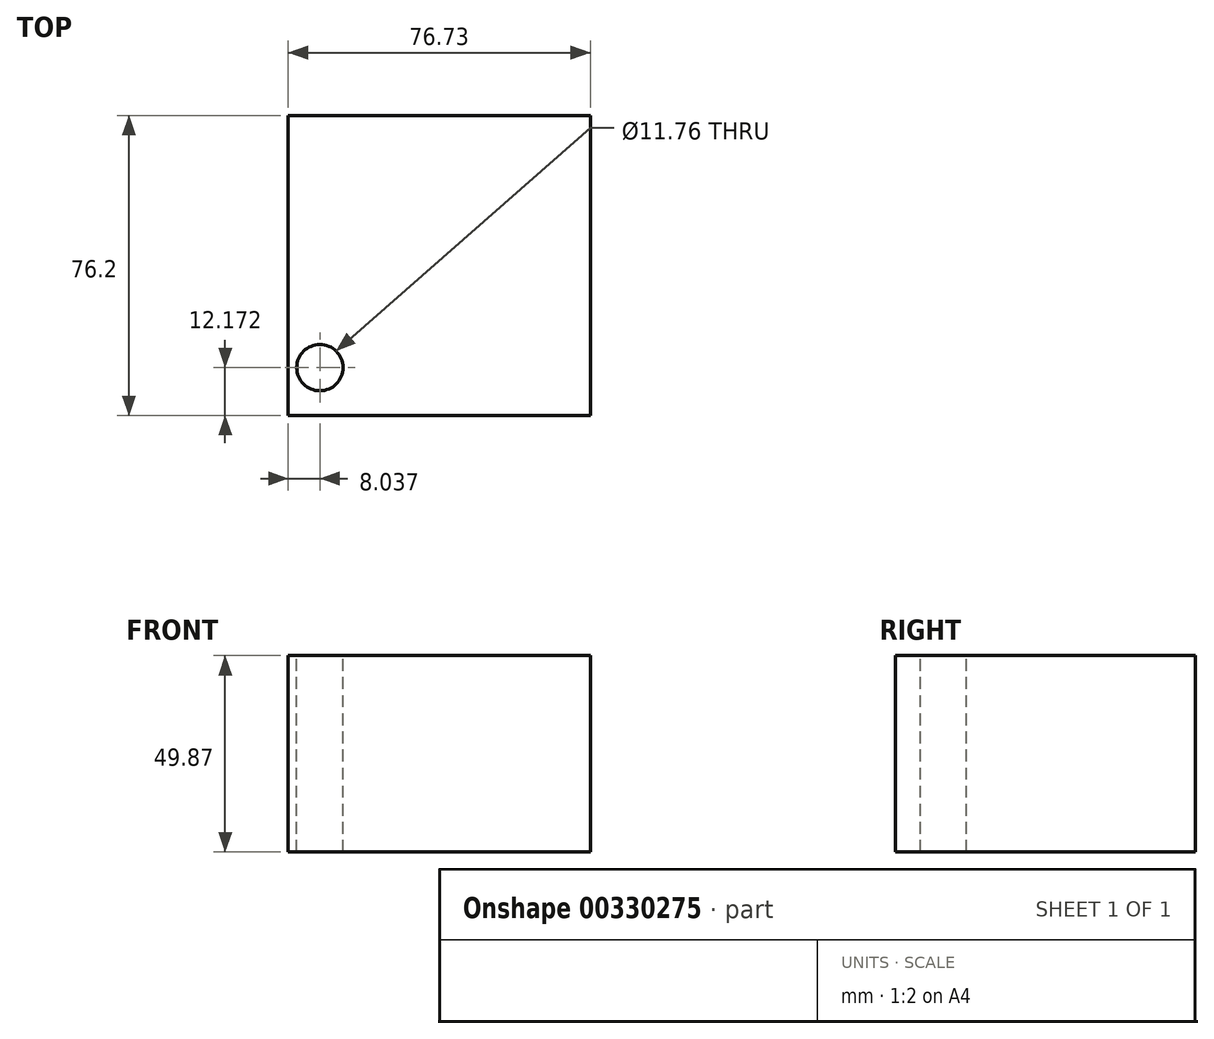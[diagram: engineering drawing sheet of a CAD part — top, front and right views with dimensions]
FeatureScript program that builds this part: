
annotation { "Feature Type Name" : "Feature", "Feature Type Description" : "" }
export const myFeature = defineFeature(function(context is Context, id is Id, definition is map)
    precondition{}
    {
        {
            var Q0;
            Q0=qCreatedBy(makeId("Front.planeOp"),FACE);
            var sketch = newSketch(context, id + "F0", { "sketchPlane" : qUnion([Q0])});
            skLineSegment(sketch, "E0.bottom", {"start": v(-55.55, 20.21) * mm, "end": v(21.18, 20.21) * mm});
            skLineSegment(sketch, "E0.top", {"start": v(-55.55, -29.66) * mm, "end": v(21.18, -29.66) * mm});
            skLineSegment(sketch, "E0.left", {"start": v(-55.55, 20.21) * mm, "end": v(-55.55, -29.66) * mm});
            skLineSegment(sketch, "E0.right", {"start": v(21.18, 20.21) * mm, "end": v(21.18, -29.66) * mm});
            skSolve(sketch);
        }
        {
            var Q0;
            Q0 = qSketchRegion(id + "F0", true);
            extrude(context, id + "F1", {"entities" : qUnion([Q0]), "depth" : -76.2 * mm});
        }
        {
            var Q0;
            Q0=makeQuery(id+"F1.opExtrude","SWEPT_FACE",FACE,{"disambiguationData":[OSD([sQuery(id+"F0.wireOp",EDGE,"E0.bottom")])]});
            var sketch = newSketch(context, id + "F2", { "sketchPlane" : qUnion([Q0])});
            skCircle(sketch, "E1", {"center": v(-47.51, 12.17) * mm, "radius": 5.88 * mm});
            skSolve(sketch);
        }
        {
            var Q0;
            Q0 = qSketchRegion(id + "F2", true);
            extrude(context, id + "F3", {"entities" : qUnion([Q0]), "operationType" : NewBodyOperationType.REMOVE, "oppositeDirection" : true, "depth" : 50.8 * mm});
        }
    });
